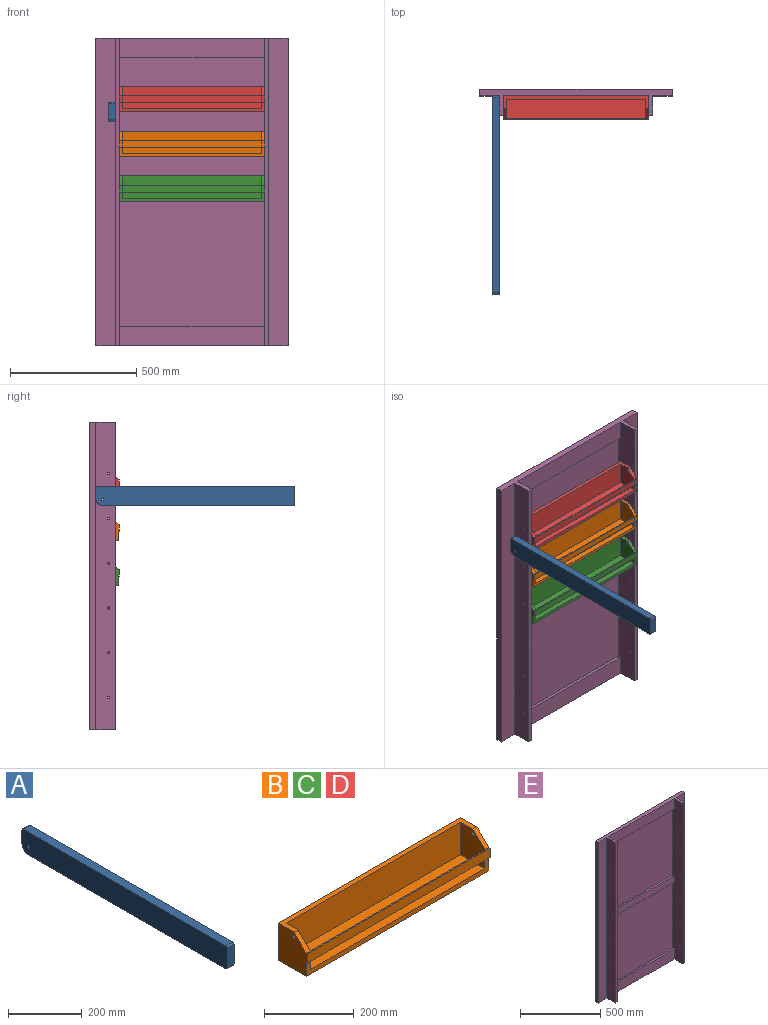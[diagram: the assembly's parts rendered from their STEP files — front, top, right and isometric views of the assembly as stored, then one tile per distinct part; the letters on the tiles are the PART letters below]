
ASSEMBLY  parts=5 mates=7
PART A: 11 faces, bbox 25.4x787.4x76.2 mm
  f0: plane 755.65x25.4mm, normal (0,0,-1), area 19193.5mm2, adj f1,f7,f9,f10
  f1: cylinder r=6.35mm len=25.4mm, axis (1,0,0), area 253.4mm2, adj f0,f2,f9,f10
  f2: plane 63.5x25.4mm, normal (0,-1,0), area 1612.9mm2, adj f1,f3,f9,f10
  f3: cylinder r=6.35mm len=25.4mm, axis (1,0,0), area 253.4mm2, adj f2,f4,f9,f10
  f4: plane 774.7x25.4mm, normal (0,0,1), area 19677.4mm2, adj f3,f5,f9,f10
  f5: cylinder r=6.35mm len=25.4mm, axis (1,0,0), area 253.4mm2, adj f4,f6,f9,f10
  f6: plane 44.45x25.4mm, normal (0,1,0), area 1129mm2, adj f5,f7,f9,f10
  f7: cylinder r=25.4mm len=25.4mm, axis (1,0,0), area 1013.4mm2, adj f0,f6,f9,f10
  f8: cylinder r=4.22mm len=25.4mm, axis (1,0,0), area 672.9mm2, adj f9,f10
  f9: plane 787.4x76.2mm, normal (-1,0,0), area 59779.6mm2, adj f0,f1,f2,f3,f4,f5,f6,f7
  f10: plane 787.4x76.2mm, normal (1,0,0), area 59779.6mm2, adj f0,f1,f2,f3,f4,f5,f6,f7
PART B: 18 faces, bbox 577.9x92.1x101.6 mm
  f0: plane 577.85x38.1mm, normal (0,-1,0), area 7983.9mm2, adj f3,f8,f9,f10,f11,f13,f16
  f1: plane 38.1x38.1mm, normal (0,-0.71,0.71), area 684.3mm2, adj f5,f8,f10,f15
  f2: cylinder r=4.22mm len=12.7mm, axis (-1,0,0), area 336.5mm2, adj f8,f10
  f3: plane 577.85x88.9mm, normal (0,0,-1), area 51370.9mm2, adj f0,f4,f8,f9
  f4: plane 577.85x101.6mm, normal (0,1,0), area 58709.6mm2, adj f3,f5,f8,f9
  f5: plane 577.85x50.8mm, normal (0,0,1), area 8306.4mm2, adj f1,f4,f6,f8,f9,f10,f11,f12
  f6: plane 38.1x38.1mm, normal (0,-0.71,0.71), area 684.3mm2, adj f5,f9,f11,f15
  f7: cylinder r=4.22mm len=12.7mm, axis (-1,0,0), area 336.5mm2, adj f9,f11
  f8: plane 101.6x92.08mm, normal (1,0,0), area 8331.2mm2, adj f0,f1,f2,f3,f4,f5,f15,f16
  f9: plane 101.6x92.08mm, normal (-1,0,0), area 8331.2mm2, adj f0,f3,f4,f5,f6,f7,f15,f16
  f10: plane 88.9x76.2mm, normal (-1,0,0), area 5992.5mm2, adj f0,f1,f2,f5,f12,f13,f14
  f11: plane 88.9x76.2mm, normal (1,0,0), area 5992.5mm2, adj f0,f5,f6,f7,f12,f13,f14
  f12: plane 552.45x88.9mm, normal (0,-1,0), area 49112.8mm2, adj f5,f10,f11,f13
  f13: plane 552.45x76.2mm, normal (0,0,1), area 42096.7mm2, adj f0,f10,f11,f12
  f14: plane 552.45x25.4mm, normal (0,1,0), area 14032.2mm2, adj f10,f11,f15,f16
  f15: plane 577.85x3.18mm, normal (0,0,1), area 1834.7mm2, adj f1,f6,f8,f9,f14,f17
  f16: plane 577.85x3.18mm, normal (0,0,-1), area 1834.7mm2, adj f0,f8,f9,f14,f17
  f17: plane 577.85x25.4mm, normal (0,-1,0), area 14677.4mm2, adj f8,f9,f15,f16
PART C: same geometry as B
PART D: same geometry as B
PART E: 44 faces, bbox 762x101.6x1219.2 mm
  f0: plane 577.85x508mm, normal (0,-1,0), area 293524.6mm2, adj f12,f13,f14,f15,f16,f17,f24,f27
  f1: plane 577.85x508mm, normal (0,-1,0), area 293524.6mm2, adj f18,f19,f20,f21,f22,f23,f24,f27
  f2: plane 577.85x78.05mm, normal (0,-1,0), area 44043.8mm2, adj f8,f14,f15,f16,f24,f27
  f3: plane 577.85x54.51mm, normal (0,-1,0), area 29378mm2, adj f12,f13,f17,f18,f19,f20,f24,f27
  f4: plane 577.85x78.05mm, normal (0,-1,0), area 44043.8mm2, adj f10,f21,f22,f23,f24,f27
  f5: plane 1219.2x76.2mm, normal (0,-1,0), area 92903mm2, adj f7,f8,f10,f25
  f6: plane 1219.2x76.2mm, normal (0,-1,0), area 92903mm2, adj f8,f9,f10,f28
  f7: plane 1219.2x25.4mm, normal (-1,0,0), area 30967.7mm2, adj f5,f8,f10,f11
  f8: plane 762x101.6mm, normal (0,0,-1), area 21774.1mm2, adj f2,f5,f6,f7,f9,f11,f24,f25
  f9: plane 1219.2x25.4mm, normal (1,0,0), area 30967.7mm2, adj f6,f8,f10,f11
  f10: plane 762x101.6mm, normal (0,0,1), area 21774.1mm2, adj f4,f5,f6,f7,f9,f11,f24,f25
  f11: plane 1219.2x762mm, normal (0,1,0), area 929030.4mm2, adj f7,f8,f9,f10
  f12: plane 558.8x12.7mm, normal (0,0,-1), area 7096.8mm2, adj f0,f3,f13,f17
  f13: cylinder r=25.4mm len=12.7mm, axis (0,-1,0), area 124mm2, adj f0,f3,f12,f24
  f14: cylinder r=25.4mm len=12.7mm, axis (0,-1,0), area 124mm2, adj f0,f2,f15,f24
  f15: plane 558.8x12.7mm, normal (0,0,1), area 7096.8mm2, adj f0,f2,f14,f16
  f16: cylinder r=25.4mm len=12.7mm, axis (0,-1,0), area 124mm2, adj f0,f2,f15,f27
  f17: cylinder r=25.4mm len=12.7mm, axis (0,-1,0), area 124mm2, adj f0,f3,f12,f27
  f18: cylinder r=25.4mm len=12.7mm, axis (0,-1,0), area 124mm2, adj f1,f3,f19,f24
  f19: plane 558.8x12.7mm, normal (0,0,1), area 7096.8mm2, adj f1,f3,f18,f20
  f20: cylinder r=25.4mm len=12.7mm, axis (0,-1,0), area 124mm2, adj f1,f3,f19,f27
  f21: cylinder r=25.4mm len=12.7mm, axis (0,-1,0), area 124mm2, adj f1,f4,f22,f27
  f22: plane 558.8x12.7mm, normal (0,0,-1), area 7096.8mm2, adj f1,f4,f21,f23
  f23: cylinder r=25.4mm len=12.7mm, axis (0,-1,0), area 124mm2, adj f1,f4,f22,f24
  f24: plane 1219.2x88.9mm, normal (1,0,0), area 105321.1mm2, adj f0,f1,f2,f3,f4,f8,f10,f13
  f25: plane 1219.2x76.2mm, normal (-1,0,0), area 92512.1mm2, adj f5,f8,f10,f26,f31,f33,f35,f37
  f26: plane 1219.2x15.88mm, normal (0,-1,0), area 19354.8mm2, adj f8,f10,f24,f25
  f27: plane 1219.2x88.9mm, normal (-1,0,0), area 105321.1mm2, adj f0,f1,f2,f3,f4,f8,f10,f16
  f28: plane 1219.2x76.2mm, normal (1,0,0), area 92512.1mm2, adj f6,f8,f10,f29,f30,f32,f34,f36
  f29: plane 1219.2x15.88mm, normal (0,-1,0), area 19354.8mm2, adj f8,f10,f27,f28
  f30: cylinder r=4.22mm len=15.88mm, axis (-1,0,0), area 420.6mm2, adj f27,f28
  f31: cylinder r=4.22mm len=15.88mm, axis (-1,0,0), area 420.6mm2, adj f24,f25
  f32: cylinder r=4.22mm len=15.88mm, axis (-1,0,0), area 420.6mm2, adj f27,f28
  f33: cylinder r=4.22mm len=15.88mm, axis (-1,0,0), area 420.6mm2, adj f24,f25
  f34: cylinder r=4.22mm len=15.88mm, axis (-1,0,0), area 420.6mm2, adj f27,f28
  f35: cylinder r=4.22mm len=15.88mm, axis (-1,0,0), area 420.6mm2, adj f24,f25
  f36: cylinder r=4.22mm len=15.88mm, axis (-1,0,0), area 420.6mm2, adj f27,f28
  f37: cylinder r=4.22mm len=15.88mm, axis (-1,0,0), area 420.6mm2, adj f24,f25
  f38: cylinder r=4.22mm len=15.88mm, axis (-1,0,0), area 420.6mm2, adj f27,f28
  f39: cylinder r=4.22mm len=15.88mm, axis (-1,0,0), area 420.6mm2, adj f24,f25
  f40: cylinder r=4.22mm len=15.88mm, axis (-1,0,0), area 420.6mm2, adj f27,f28
  f41: cylinder r=4.22mm len=15.88mm, axis (-1,0,0), area 420.6mm2, adj f24,f25
  f42: cylinder r=4.22mm len=15.88mm, axis (-1,0,0), area 420.6mm2, adj f27,f28
  f43: cylinder r=4.22mm len=15.88mm, axis (-1,0,0), area 420.6mm2, adj f24,f25
PLACE A rot(axis=(-1,0,0),0deg) t=(0,0,0)mm
PLACE B t=(0,0,-177.8)mm
PLACE C t=(0,0,-355.6)mm
PLACE D rot(axis=(-1,0,0),0deg) t=(0,0,0)mm
PLACE E rot(axis=(-1,0,0),0deg) t=(0,0,0)mm
MATE revolute A.f7 <-> E.f42  axis (1,0,0) through (-304.8,-50.8,914.4)mm
MATE parallel D.f3 <-> A.f0  axis (0,0,-1) through (0,-69.85,927.1)mm
MATE parallel D.f3 <-> B.f3  axis (0,0,-1) through (0,-69.85,927.1)mm
MATE revolute E.f32 <-> B.f2  axis (1,0,0) through (-288.93,-76.2,838.2)mm
MATE revolute D.f2 <-> E.f30  axis (-1,0,0) through (-288.93,-76.2,1016)mm
MATE revolute C.f2 <-> E.f34  axis (-1,0,0) through (-288.93,-76.2,660.4)mm
MATE parallel D.f3 <-> C.f3  axis (0,0,-1) through (288.92,-25.4,927.1)mm
